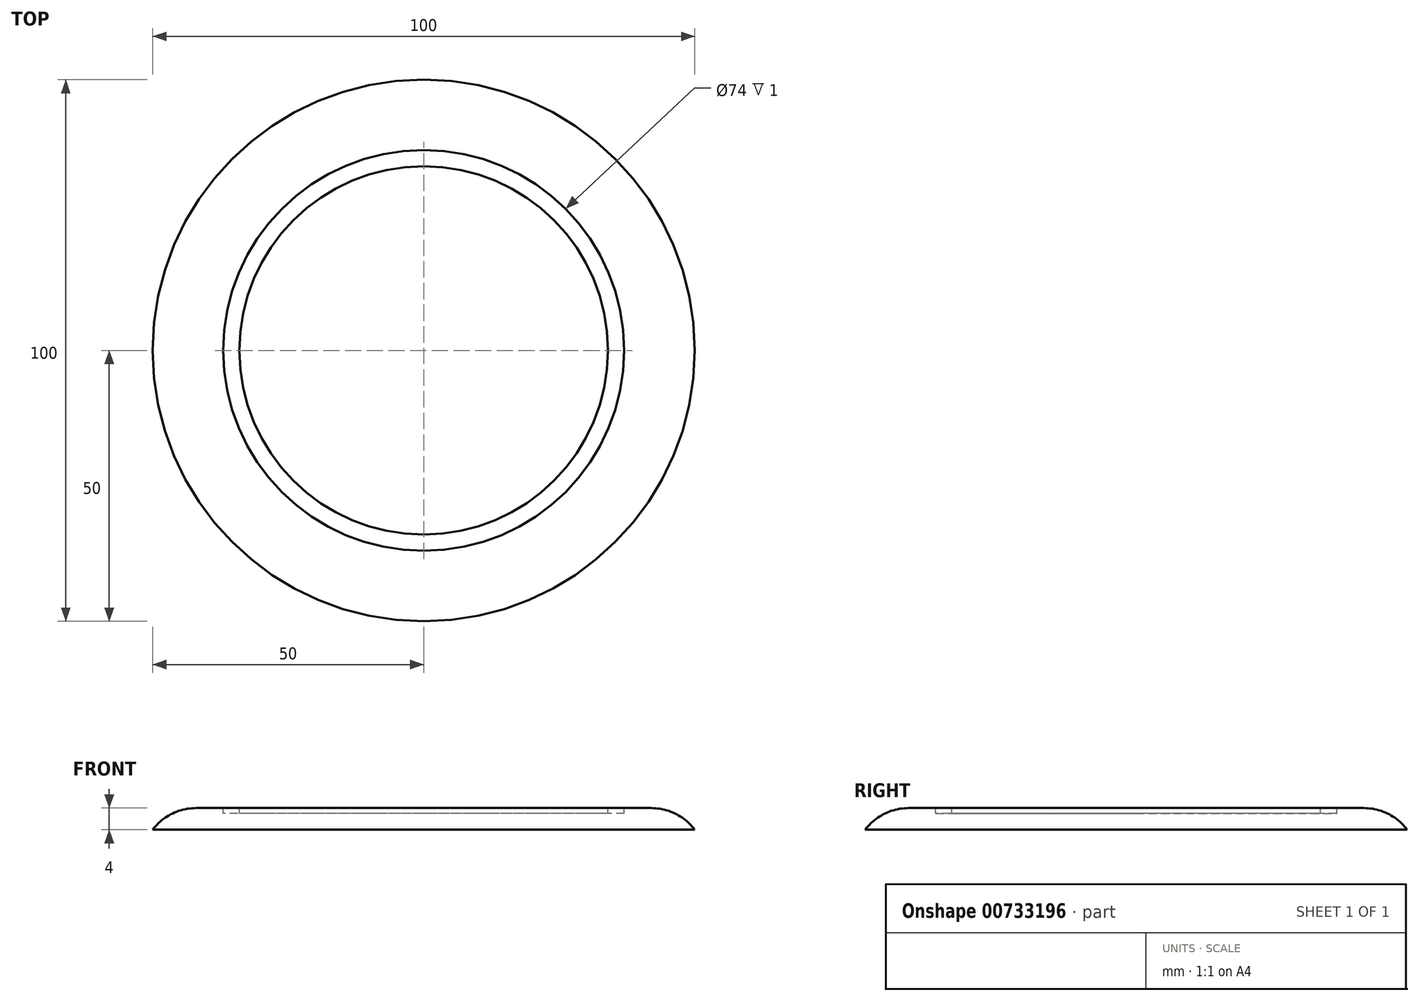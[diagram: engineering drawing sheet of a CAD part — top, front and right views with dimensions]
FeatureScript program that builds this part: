
annotation { "Feature Type Name" : "Feature", "Feature Type Description" : "" }
export const myFeature = defineFeature(function(context is Context, id is Id, definition is map)
    precondition{}
    {
        {
            var Q0;
            Q0=qCreatedBy(makeId("Top.planeOp"),FACE);
            var sketch = newSketch(context, id + "F0", { "sketchPlane" : qUnion([Q0])});
            skCircle(sketch, "E0", {"center": v(0, 0) * mm, "radius": 50 * mm});
            skSolve(sketch);
        }
        {
            var Q0;
            Q0=makeQuery(id+"F0.imprint","IMPRINT",FACE,{"disambiguationData":[TD([[makeQuery(id+"F0.imprint","IMPRINT",EDGE,{"derivedFrom":sQuery(id+"F0.wireOp",EDGE,"E0")}),1.0]])]});
            extrude(context, id + "F1", {"entities" : qUnion([Q0]), "depth" : 4 * mm, "offsetDistance" : 25 * mm});
        }
        {
            var Q0;
            Q0=makeQuery(id+"F1.opExtrude","CAP_EDGE",EDGE,{"disambiguationData":[OSD([sQuery(id+"F0.wireOp",EDGE,"E0")])],"isStart":false});
            fillet(context, id + "F2", {"entities" : qUnion([Q0]), "radius" : 10 * mm, "tangentPropagation" : true, "allowEdgeOverflow" : false});
        }
        {
            var Q0;
            Q0=makeQuery(id+"F1.opExtrude","CAP_FACE",FACE,{"disambiguationData":[OSD([sQuery(id+"F0.wireOp",EDGE,"E0")])],"isStart":false});
            var sketch = newSketch(context, id + "F3", { "sketchPlane" : qUnion([Q0])});
            skCircle(sketch, "E1", {"center": v(0, 0) * mm, "radius": 37 * mm});
            skCircle(sketch, "E2", {"center": v(0, 0) * mm, "radius": 34 * mm});
            skSolve(sketch);
        }
        {
            var Q0;
            Q0=makeQuery(id+"F3.imprint","IMPRINT",FACE,{"disambiguationData":[TD([[makeQuery(id+"F3.imprint","IMPRINT",EDGE,{"derivedFrom":sQuery(id+"F3.wireOp",EDGE,"E1")}),1.0]])]});
            extrude(context, id + "F4", {"entities" : qUnion([Q0]), "operationType" : NewBodyOperationType.REMOVE, "oppositeDirection" : true, "depth" : 1 * mm, "offsetDistance" : 25 * mm});
        }
    });
